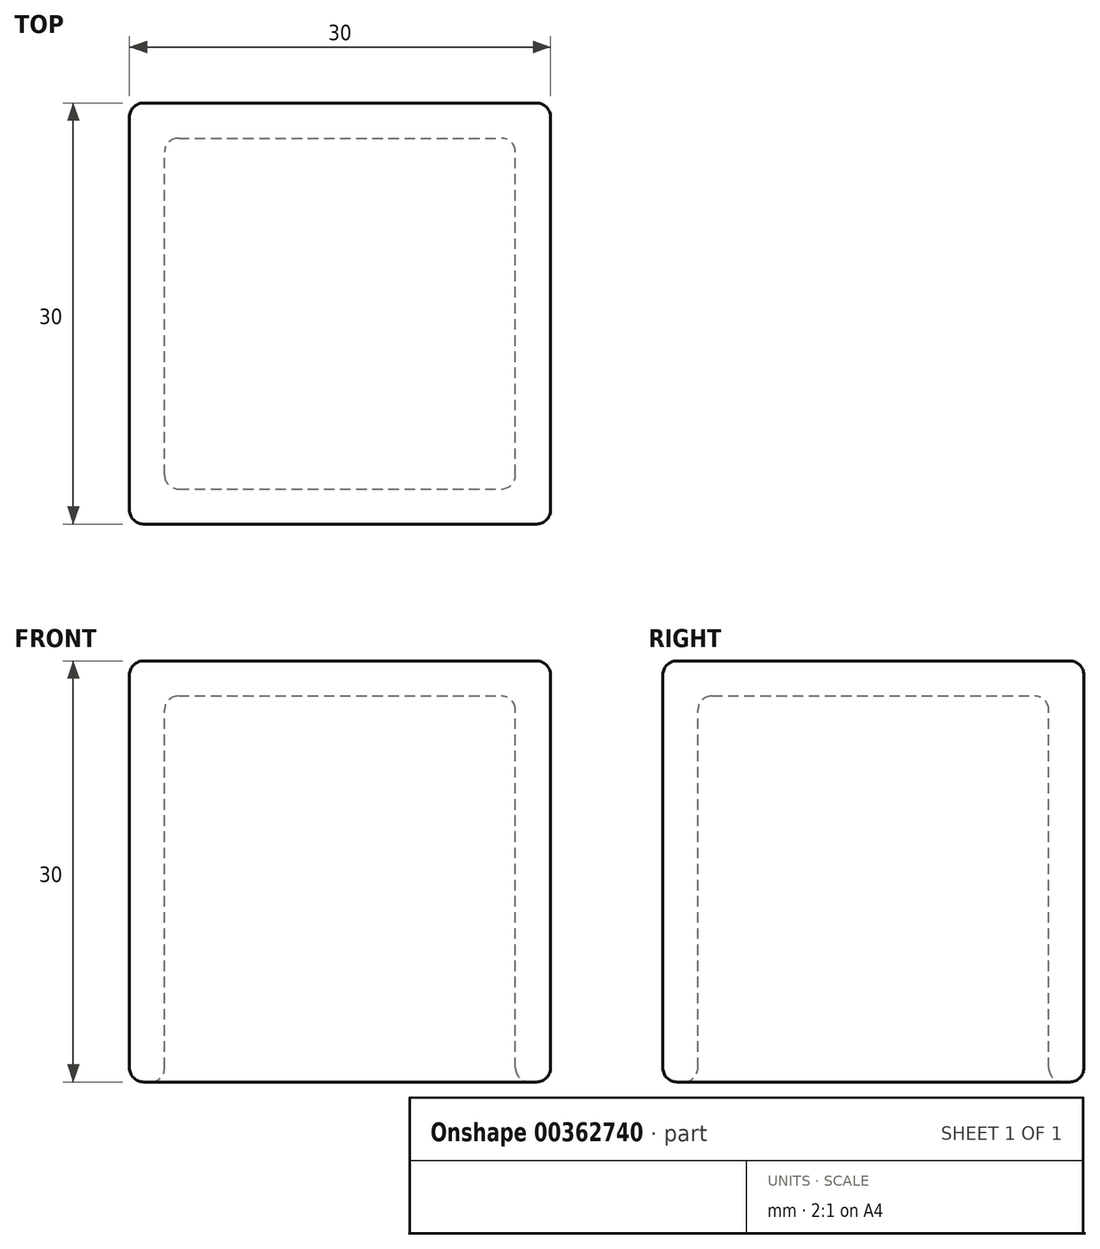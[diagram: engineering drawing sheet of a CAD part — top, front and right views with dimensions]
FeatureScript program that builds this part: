
annotation { "Feature Type Name" : "Feature", "Feature Type Description" : "" }
export const myFeature = defineFeature(function(context is Context, id is Id, definition is map)
    precondition{}
    {
        {
            var Q0;
            Q0=qCreatedBy(makeId("Front.planeOp"),FACE);
            var sketch = newSketch(context, id + "F0", { "sketchPlane" : qUnion([Q0])});
            skLineSegment(sketch, "E0.bottom", {"start": v(0, 0) * mm, "end": v(30, 0) * mm});
            skLineSegment(sketch, "E0.top", {"start": v(0, 30) * mm, "end": v(30, 30) * mm});
            skLineSegment(sketch, "E0.left", {"start": v(0, 0) * mm, "end": v(0, 30) * mm});
            skLineSegment(sketch, "E0.right", {"start": v(30, 0) * mm, "end": v(30, 30) * mm});
            skSolve(sketch);
        }
        {
            var Q0;
            Q0 = qSketchRegion(id + "F0", true);
            extrude(context, id + "F1", {"entities" : qUnion([Q0]), "depth" : 30 * mm});
        }
        {
            var Q0;
            Q0=makeQuery(id+"F1.opExtrude","SWEPT_FACE",FACE,{"disambiguationData":[OSD([sQuery(id+"F0.wireOp",EDGE,"E0.bottom")])]});
            shell(context, id + "F2", {"entities" : qUnion([Q0]), "thickness" : 2.5 * mm});
        }
        {
            var Q0;
            Q0=makeQuery(id+"F1.opExtrude","SWEPT_EDGE",EDGE,{"disambiguationData":[OSD([sQuery(id+"F0.wireOp",EDGE,"E0.top"),sQuery(id+"F0.wireOp",EDGE,"E0.right")])]});
            var Q1;
            Q1=makeQuery(id+"F1.opExtrude","SWEPT_EDGE",EDGE,{"disambiguationData":[OSD([sQuery(id+"F0.wireOp",EDGE,"E0.bottom"),sQuery(id+"F0.wireOp",EDGE,"E0.right")])]});
            var Q2;
            Q2=makeQuery(id+"F1.opExtrude","SWEPT_EDGE",EDGE,{"disambiguationData":[OSD([sQuery(id+"F0.wireOp",EDGE,"E0.bottom"),sQuery(id+"F0.wireOp",EDGE,"E0.left")])]});
            var Q3;
            Q3=makeQuery(id+"F2.opShell","OFFSET_EDGE",EDGE,{"disambiguationData":[OSD([sQuery(id+"F0.wireOp",EDGE,"E0.bottom"),sQuery(id+"F0.wireOp",EDGE,"E0.left")])]});
            var Q4;
            Q4=makeQuery(id+"F1.opExtrude","CAP_EDGE",EDGE,{"disambiguationData":[OSD([sQuery(id+"F0.wireOp",EDGE,"E0.bottom")])],"isStart":true});
            var Q5;
            Q5=makeQuery(id+"F1.opExtrude","CAP_EDGE",EDGE,{"disambiguationData":[OSD([sQuery(id+"F0.wireOp",EDGE,"E0.bottom")])],"isStart":false});
            var Q6;
            Q6=makeQuery(id+"F1.opExtrude","CAP_EDGE",EDGE,{"disambiguationData":[OSD([sQuery(id+"F0.wireOp",EDGE,"E0.top")])],"isStart":true});
            var Q7;
            Q7=makeQuery(id+"F2.opShell","OFFSET_EDGE",EDGE,{"disambiguationData":[OSD([sQuery(id+"F0.wireOp",EDGE,"E0.bottom"),sQuery(id+"F0.wireOp",EDGE,"E0.right")])]});
            var Q8;
            Q8=makeQuery(id+"F2.opShell","OFFSET_EDGE",EDGE,{"disambiguationData":[OSD([sQuery(id+"F0.wireOp",EDGE,"E0.top"),sQuery(id+"F0.wireOp",EDGE,"E0.left")])]});
            var Q9;
            {var subQ0=sQuery(id+"F0.wireOp",EDGE,"E0.bottom");Q9=makeQuery(id+"F2.opShell","OFFSET_EDGE",EDGE,{"disambiguationData":[OSD([subQ0]),TDD([makeQuery(id+"F1.opExtrude","CAP_EDGE",EDGE,{"disambiguationData":[OSD([subQ0])],"isStart":true})])]});}
            var Q10;
            {var subQ0=sQuery(id+"F0.wireOp",EDGE,"E0.bottom");Q10=makeQuery(id+"F2.opShell","OFFSET_EDGE",EDGE,{"disambiguationData":[OSD([subQ0]),TDD([makeQuery(id+"F1.opExtrude","CAP_EDGE",EDGE,{"disambiguationData":[OSD([subQ0])],"isStart":false})])]});}
            var Q11;
            Q11=makeQuery(id+"F1.opExtrude","SWEPT_EDGE",EDGE,{"disambiguationData":[OSD([sQuery(id+"F0.wireOp",EDGE,"E0.top"),sQuery(id+"F0.wireOp",EDGE,"E0.left")])]});
            var Q12;
            Q12=makeQuery(id+"F1.opExtrude","CAP_EDGE",EDGE,{"disambiguationData":[OSD([sQuery(id+"F0.wireOp",EDGE,"E0.top")])],"isStart":false});
            var Q13;
            Q13=makeQuery(id+"F1.opExtrude","CAP_EDGE",EDGE,{"disambiguationData":[OSD([sQuery(id+"F0.wireOp",EDGE,"E0.left")])],"isStart":true});
            var Q14;
            Q14=makeQuery(id+"F1.opExtrude","CAP_EDGE",EDGE,{"disambiguationData":[OSD([sQuery(id+"F0.wireOp",EDGE,"E0.left")])],"isStart":false});
            var Q15;
            Q15=makeQuery(id+"F1.opExtrude","CAP_EDGE",EDGE,{"disambiguationData":[OSD([sQuery(id+"F0.wireOp",EDGE,"E0.right")])],"isStart":true});
            var Q16;
            Q16=makeQuery(id+"F1.opExtrude","CAP_EDGE",EDGE,{"disambiguationData":[OSD([sQuery(id+"F0.wireOp",EDGE,"E0.right")])],"isStart":false});
            var Q17;
            Q17=makeQuery(id+"F2.opShell","OFFSET_EDGE",EDGE,{"disambiguationData":[OSD([sQuery(id+"F0.wireOp",EDGE,"E0.top"),sQuery(id+"F0.wireOp",EDGE,"E0.right")])]});
            var Q18;
            {var subQ0=sQuery(id+"F0.wireOp",EDGE,"E0.top");Q18=makeQuery(id+"F2.opShell","OFFSET_EDGE",EDGE,{"disambiguationData":[OSD([subQ0]),TDD([makeQuery(id+"F1.opExtrude","CAP_EDGE",EDGE,{"disambiguationData":[OSD([subQ0])],"isStart":true})])]});}
            var Q19;
            {var subQ0=sQuery(id+"F0.wireOp",EDGE,"E0.top");Q19=makeQuery(id+"F2.opShell","OFFSET_EDGE",EDGE,{"disambiguationData":[OSD([subQ0]),TDD([makeQuery(id+"F1.opExtrude","CAP_EDGE",EDGE,{"disambiguationData":[OSD([subQ0])],"isStart":false})])]});}
            var Q20;
            {var subQ0=sQuery(id+"F0.wireOp",EDGE,"E0.left");Q20=makeQuery(id+"F2.opShell","OFFSET_EDGE",EDGE,{"disambiguationData":[OSD([subQ0]),TDD([makeQuery(id+"F1.opExtrude","CAP_EDGE",EDGE,{"disambiguationData":[OSD([subQ0])],"isStart":true})])]});}
            var Q21;
            {var subQ0=sQuery(id+"F0.wireOp",EDGE,"E0.left");Q21=makeQuery(id+"F2.opShell","OFFSET_EDGE",EDGE,{"disambiguationData":[OSD([subQ0]),TDD([makeQuery(id+"F1.opExtrude","CAP_EDGE",EDGE,{"disambiguationData":[OSD([subQ0])],"isStart":false})])]});}
            var Q22;
            {var subQ0=sQuery(id+"F0.wireOp",EDGE,"E0.right");Q22=makeQuery(id+"F2.opShell","OFFSET_EDGE",EDGE,{"disambiguationData":[OSD([subQ0]),TDD([makeQuery(id+"F1.opExtrude","CAP_EDGE",EDGE,{"disambiguationData":[OSD([subQ0])],"isStart":true})])]});}
            var Q23;
            {var subQ0=sQuery(id+"F0.wireOp",EDGE,"E0.right");Q23=makeQuery(id+"F2.opShell","OFFSET_EDGE",EDGE,{"disambiguationData":[OSD([subQ0]),TDD([makeQuery(id+"F1.opExtrude","CAP_EDGE",EDGE,{"disambiguationData":[OSD([subQ0])],"isStart":false})])]});}
            fillet(context, id + "F3", {"entities" : qUnion([Q0, Q1, Q2, Q3, Q4, Q5, Q6, Q7, Q8, Q9, Q10, Q11, Q12, Q13, Q14, Q15, Q16, Q17, Q18, Q19, Q20, Q21, Q22, Q23]), "radius" : 1 * mm, "tangentPropagation" : true, "allowEdgeOverflow" : false});
        }
    });
